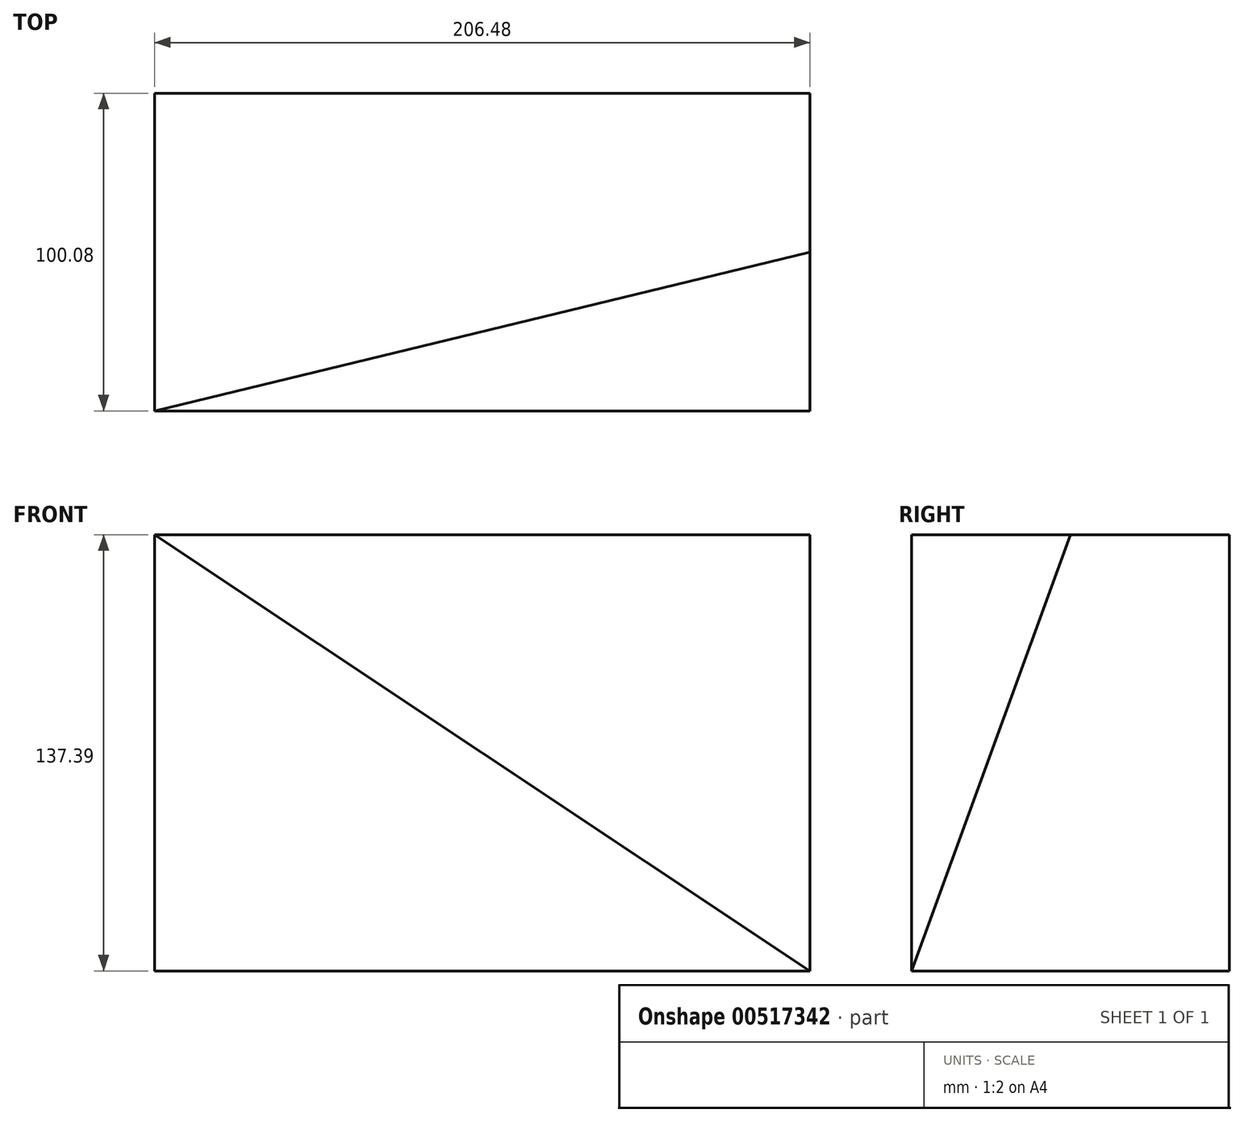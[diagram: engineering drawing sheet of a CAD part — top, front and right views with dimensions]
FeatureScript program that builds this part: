
annotation { "Feature Type Name" : "Feature", "Feature Type Description" : "" }
export const myFeature = defineFeature(function(context is Context, id is Id, definition is map)
    precondition{}
    {
        {
            var Q0;
            Q0=qCreatedBy(makeId("Front.planeOp"),FACE);
            var sketch = newSketch(context, id + "F0", { "sketchPlane" : qUnion([Q0])});
            skLineSegment(sketch, "E0.bottom", {"start": v(-125.44, 70.26) * mm, "end": v(81.04, 70.26) * mm});
            skLineSegment(sketch, "E0.top", {"start": v(-125.44, -67.13) * mm, "end": v(81.04, -67.13) * mm});
            skLineSegment(sketch, "E0.left", {"start": v(-125.44, 70.26) * mm, "end": v(-125.44, -67.13) * mm});
            skLineSegment(sketch, "E0.right", {"start": v(81.04, 70.26) * mm, "end": v(81.04, -67.13) * mm});
            skSolve(sketch);
        }
        {
            var Q0;
            Q0 = qSketchRegion(id + "F0", true);
            extrude(context, id + "F1", {"entities" : qUnion([Q0]), "depth" : 100.08 * mm, "offsetDistance" : 25.4 * mm});
        }
        {
            var Q0;
            Q0=makeQuery(id+"F1.opExtrude","SWEPT_EDGE",EDGE,{"disambiguationData":[OSD([sQuery(id+"F0.wireOp",EDGE,"E0.bottom"),sQuery(id+"F0.wireOp",EDGE,"E0.right")])]});
            cPoint(context, id + "F2", {"entities" : qUnion([Q0]), "parameter" : 0.5});
        }
        {
            var Q0;
            Q0=makeQuery(id+"F1.opExtrude","CAP_VERTEX",VERTEX,{"disambiguationData":[OSD([sQuery(id+"F0.wireOp",EDGE,"E0.bottom"),sQuery(id+"F0.wireOp",EDGE,"E0.left")])],"isStart":false});
            var Q1;
            Q1=makeQuery(id+"F1.opExtrude","CAP_VERTEX",VERTEX,{"disambiguationData":[OSD([sQuery(id+"F0.wireOp",EDGE,"E0.top"),sQuery(id+"F0.wireOp",EDGE,"E0.right")])],"isStart":false});
            var Q2;
            Q2 = qCreatedBy(id + "F2" ,VERTEX);
            cPlane(context, id + "F3", {"entities" : qUnion([Q0, Q1, Q2]), "cplaneType" : CPlaneType.THREE_POINT, "offset" : 25.4 * mm, "width" : 152.4 * mm, "height" : 152.4 * mm});
        }
        {
            var Q0;
            Q0=qCreatedBy(id+"F3.planeOp",FACE);
            var sketch = newSketch(context, id + "F4", { "sketchPlane" : qUnion([Q0])});
            skLineSegment(sketch, "E1", {"start": v(-63.24, -97.32) * mm, "end": v(148.52, 31.77) * mm});
            skLineSegment(sketch, "E2", {"start": v(-63.24, 48.9) * mm, "end": v(-63.24, -97.32) * mm});
            skLineSegment(sketch, "E3", {"start": v(148.52, 31.77) * mm, "end": v(-63.24, 48.9) * mm});
            skSolve(sketch);
        }
        {
            var Q0;
            Q0 = qSketchRegion(id + "F4", true);
            extrude(context, id + "F5", {"entities" : qUnion([Q0]), "operationType" : NewBodyOperationType.REMOVE, "endBound" : BoundingType.THROUGH_ALL, "oppositeDirection" : true, "depth" : 25.4 * mm, "offsetDistance" : 25.4 * mm});
        }
    });
